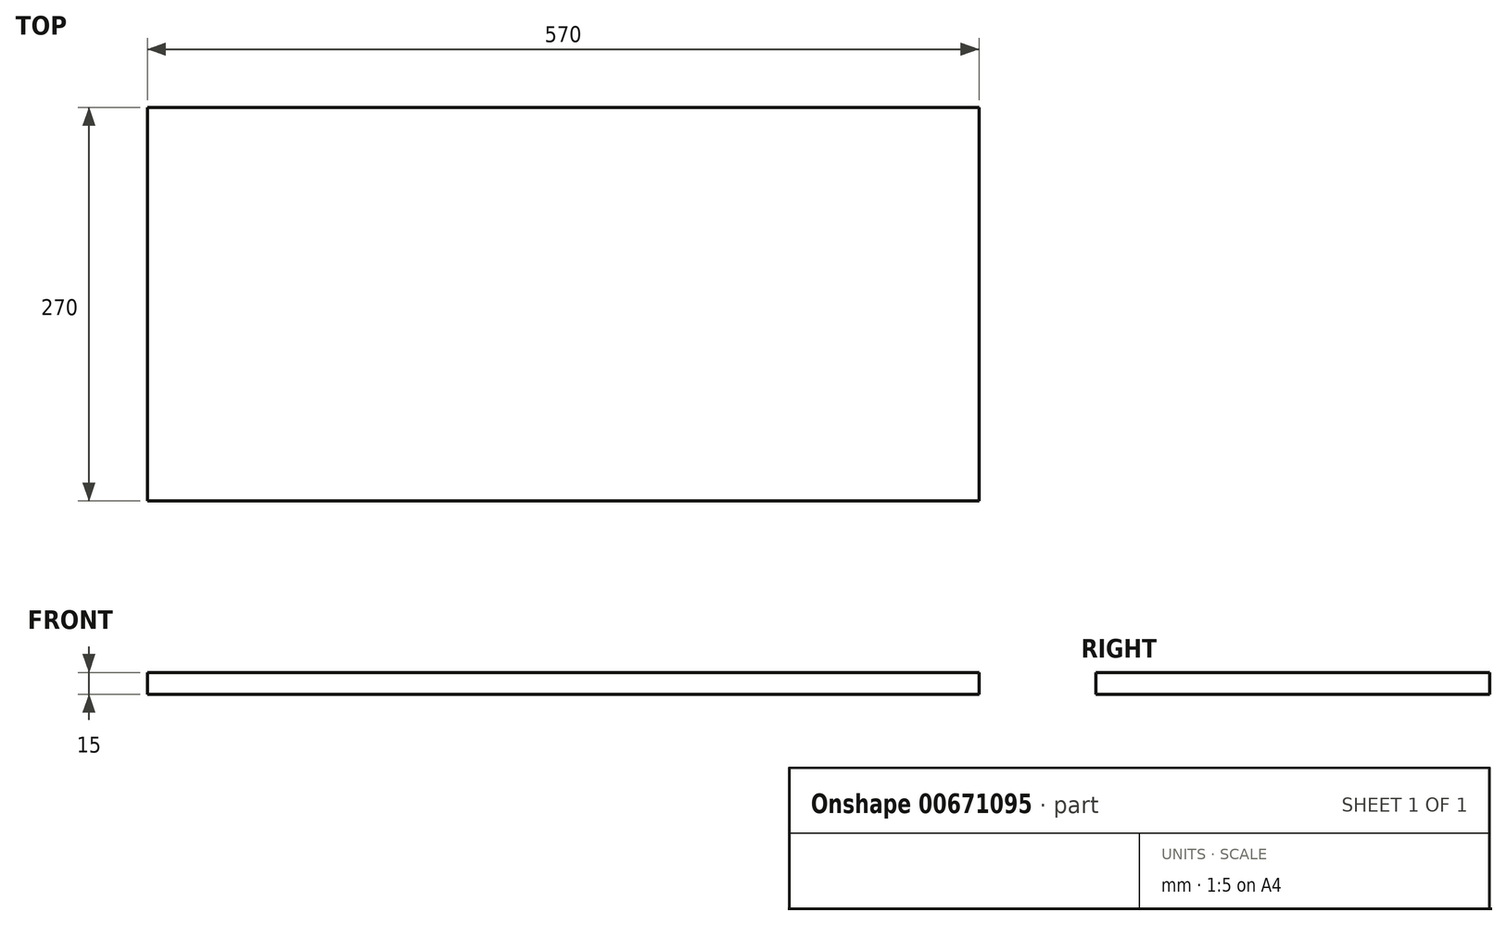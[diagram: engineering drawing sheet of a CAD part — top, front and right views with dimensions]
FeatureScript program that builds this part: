
annotation { "Feature Type Name" : "Feature", "Feature Type Description" : "" }
export const myFeature = defineFeature(function(context is Context, id is Id, definition is map)
    precondition{}
    {
        {
            var Q0;
            Q0=qCreatedBy(makeId("Top.planeOp"),FACE);
            var sketch = newSketch(context, id + "F0", { "sketchPlane" : qUnion([Q0])});
            skLineSegment(sketch, "E0.bottom", {"start": v(0, 0) * mm, "end": v(570, 0) * mm});
            skLineSegment(sketch, "E0.top", {"start": v(0, -270) * mm, "end": v(570, -270) * mm});
            skLineSegment(sketch, "E0.left", {"start": v(0, 0) * mm, "end": v(0, -270) * mm});
            skLineSegment(sketch, "E0.right", {"start": v(570, 0) * mm, "end": v(570, -270) * mm});
            skSolve(sketch);
        }
        {
            var Q0;
            Q0=makeQuery(id+"F0.imprint","IMPRINT",FACE,{"disambiguationData":[TD([[makeQuery(id+"F0.imprint","IMPRINT",EDGE,{"derivedFrom":sQuery(id+"F0.wireOp",EDGE,"E0.bottom")}),-1.0]])]});
            extrude(context, id + "F1", {"entities" : qUnion([Q0]), "depth" : 15 * mm, "offsetDistance" : 25 * mm});
        }
    });
